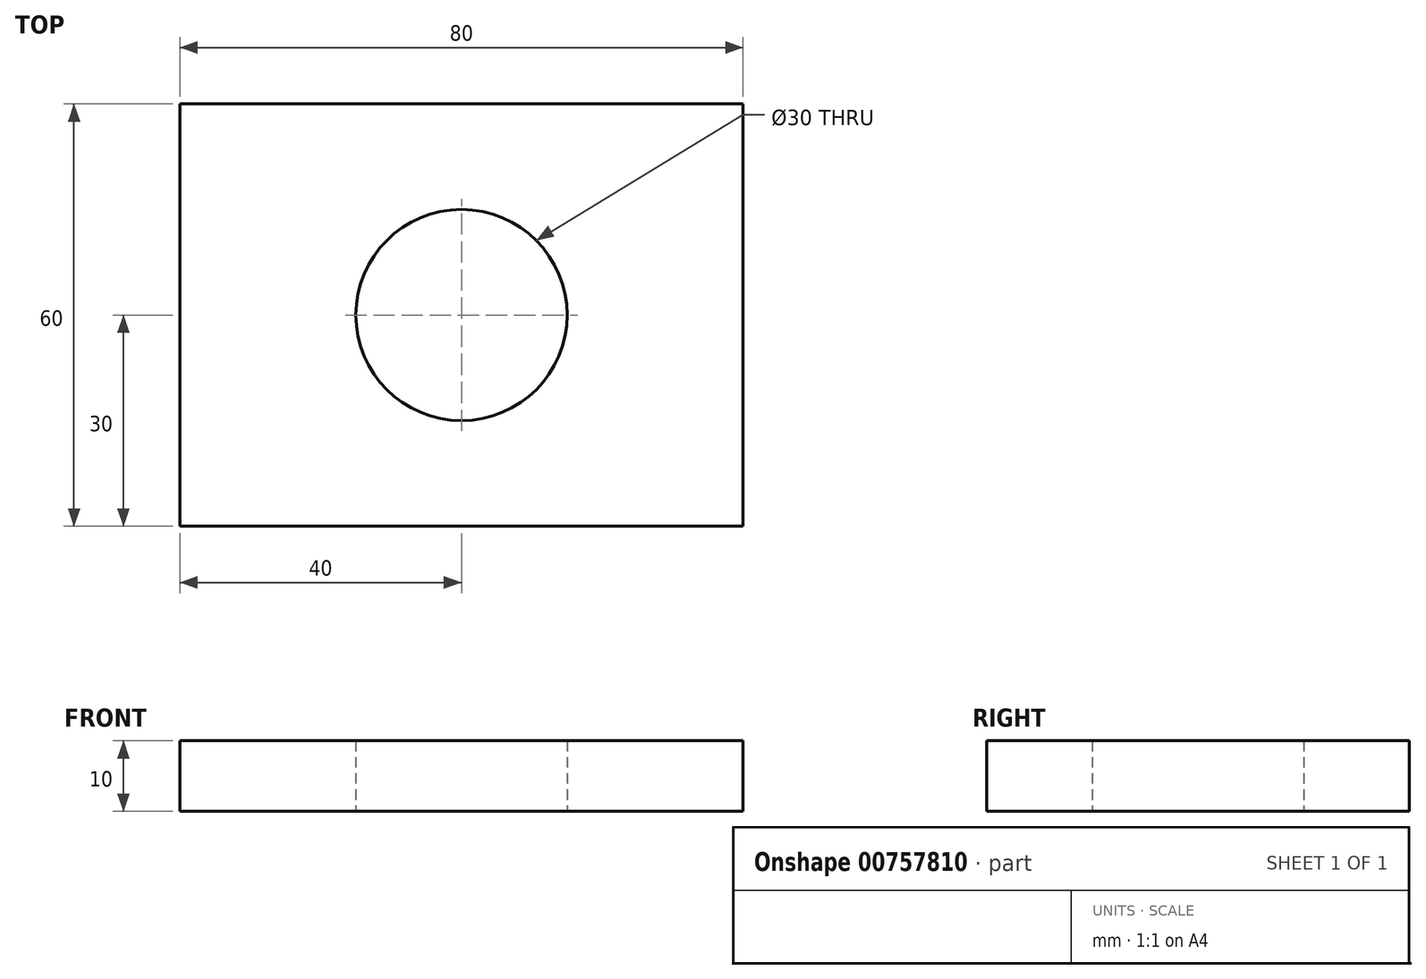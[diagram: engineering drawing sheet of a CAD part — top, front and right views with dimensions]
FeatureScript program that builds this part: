
annotation { "Feature Type Name" : "Feature", "Feature Type Description" : "" }
export const myFeature = defineFeature(function(context is Context, id is Id, definition is map)
    precondition{}
    {
        {
            var Q0;
            Q0=qCreatedBy(makeId("Top.planeOp"),FACE);
            var sketch = newSketch(context, id + "F0", { "sketchPlane" : qUnion([Q0])});
            skLineSegment(sketch, "E0", {"start": v(40, 0) * mm, "end": v(40, 30) * mm});
            skLineSegment(sketch, "E1", {"start": v(-40, 30) * mm, "end": v(-40, 0) * mm});
            skLineSegment(sketch, "E2", {"start": v(-40, -30) * mm, "end": v(40, -30) * mm});
            skLineSegment(sketch, "E3", {"start": v(40, -30) * mm, "end": v(40, 0) * mm});
            skLineSegment(sketch, "E4", {"start": v(-40, 0) * mm, "end": v(-40, -30) * mm});
            skCircle(sketch, "E5", {"center": v(0, 0) * mm, "radius": 15 * mm});
            skLineSegment(sketch, "E6", {"start": v(-40, 30) * mm, "end": v(0, 30) * mm});
            skLineSegment(sketch, "E7", {"start": v(0, 30) * mm, "end": v(40, 30) * mm});
            skSolve(sketch);
        }
        {
            var Q0;
            Q0 = qSketchRegion(id + "F0", true);
            extrude(context, id + "F1", {"entities" : qUnion([Q0]), "depth" : 10 * mm, "offsetDistance" : 25 * mm});
        }
    });
